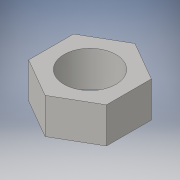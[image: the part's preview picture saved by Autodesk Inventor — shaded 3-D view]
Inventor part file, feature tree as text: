
AUTODESK INVENTOR PART (.ipt)
format: ipt  version: 2016 (Build 200138000, 138)  size: 95,232 bytes
history: native  units: in
note: dims shown in document units (in); Inventor stores cm internally (conversion verified against a paired STEP export)
features: extrude x1, sketch x1
ambient origin geometry x8: Origin, YZ Plane, XZ Plane, XY Plane, X Axis, Y Axis, Z Axis, Center Point
bodies: Solid1 (feature_tree)
feature tree (2):
  extrude  "Extrusion1"  Depth=0.3438in
  sketch  "Sketch1"  dims[d0=0.75in d1=0.5in d2=0.3438in d3=0.0in]
